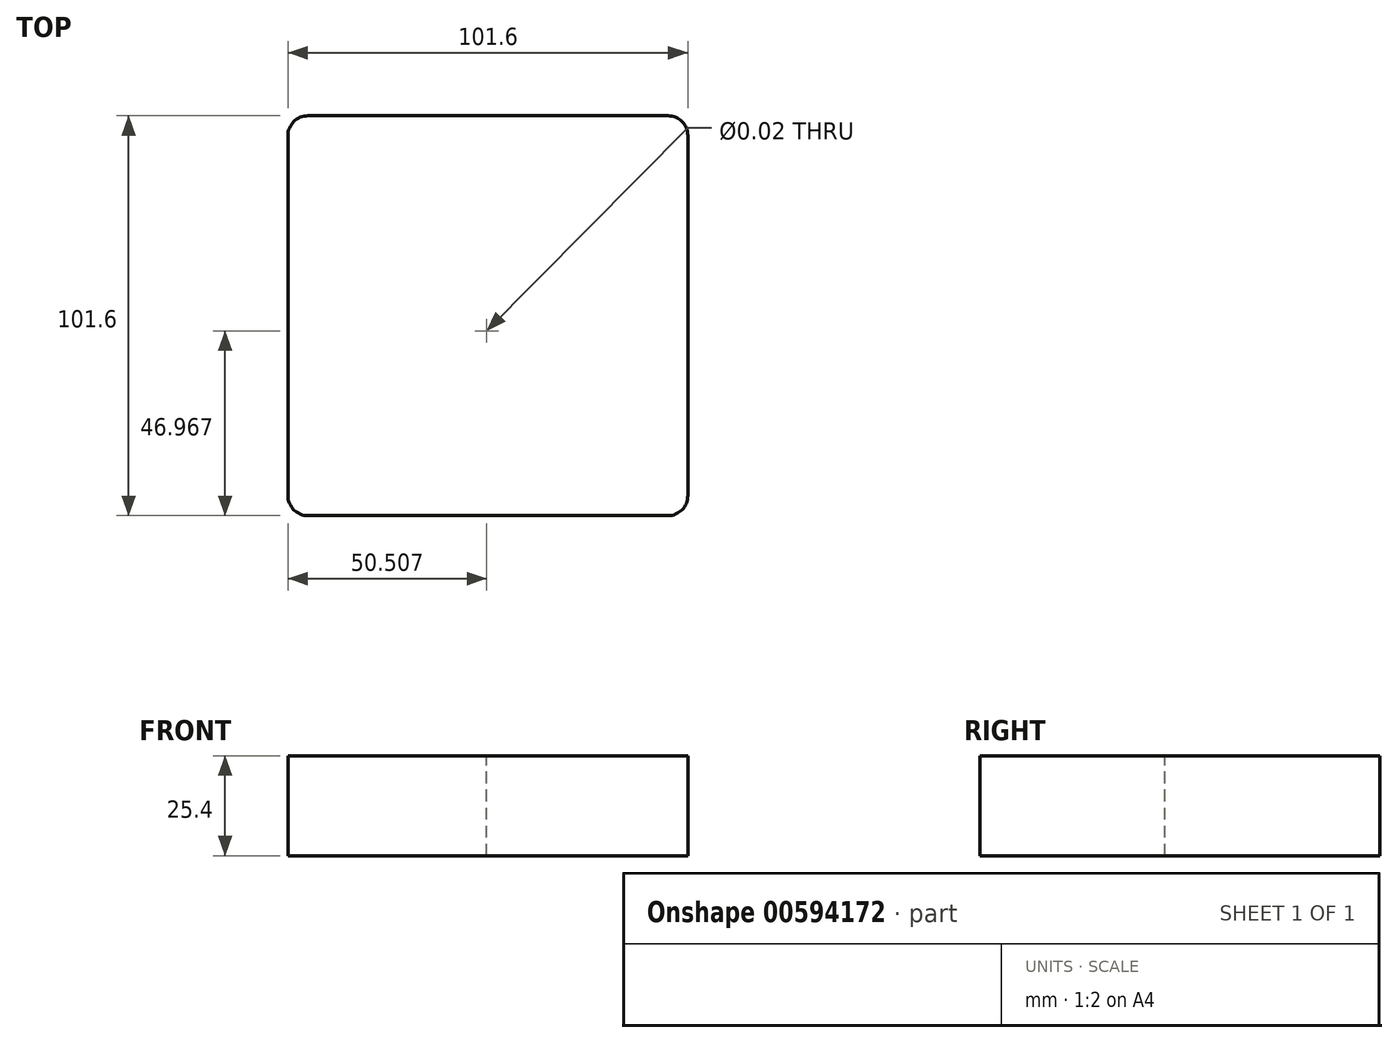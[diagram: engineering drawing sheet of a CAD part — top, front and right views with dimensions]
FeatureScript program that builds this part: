
annotation { "Feature Type Name" : "Feature", "Feature Type Description" : "" }
export const myFeature = defineFeature(function(context is Context, id is Id, definition is map)
    precondition{}
    {
        {
            var Q0;
            Q0=qCreatedBy(makeId("Top.planeOp"),FACE);
            var sketch = newSketch(context, id + "F0", { "sketchPlane" : qUnion([Q0])});
            skLineSegment(sketch, "E0.bottom", {"start": v(-75.45, 69.96) * mm, "end": v(26.15, 69.96) * mm});
            skLineSegment(sketch, "E0.top", {"start": v(-75.45, -31.64) * mm, "end": v(26.15, -31.64) * mm});
            skLineSegment(sketch, "E0.left", {"start": v(-75.45, 69.96) * mm, "end": v(-75.45, -31.64) * mm});
            skLineSegment(sketch, "E0.right", {"start": v(26.15, 69.96) * mm, "end": v(26.15, -31.64) * mm});
            skSolve(sketch);
        }
        {
            var Q0;
            Q0 = qSketchRegion(id + "F0", true);
            extrude(context, id + "F1", {"entities" : qUnion([Q0]), "depth" : 25.4 * mm, "offsetDistance" : 25.4 * mm});
        }
        {
            var Q0;
            Q0=makeQuery(id+"F1.opExtrude","SWEPT_EDGE",EDGE,{"disambiguationData":[OSD([sQuery(id+"F0.wireOp",EDGE,"E0.bottom"),sQuery(id+"F0.wireOp",EDGE,"E0.left")])]});
            fillet(context, id + "F2", {"entities" : qUnion([Q0]), "radius" : 5.08 * mm, "tangentPropagation" : true, "allowEdgeOverflow" : false});
        }
        {
            var Q0;
            Q0=makeQuery(id+"F1.opExtrude","SWEPT_EDGE",EDGE,{"disambiguationData":[OSD([sQuery(id+"F0.wireOp",EDGE,"E0.top"),sQuery(id+"F0.wireOp",EDGE,"E0.left")])]});
            fillet(context, id + "F3", {"entities" : qUnion([Q0]), "radius" : 5.08 * mm, "tangentPropagation" : true, "allowEdgeOverflow" : false});
        }
        {
            var Q0;
            Q0=makeQuery(id+"F1.opExtrude","SWEPT_EDGE",EDGE,{"disambiguationData":[OSD([sQuery(id+"F0.wireOp",EDGE,"E0.bottom"),sQuery(id+"F0.wireOp",EDGE,"E0.right")])]});
            fillet(context, id + "F4", {"entities" : qUnion([Q0]), "radius" : 5.08 * mm, "tangentPropagation" : true, "allowEdgeOverflow" : false});
        }
        {
            var Q0;
            Q0=makeQuery(id+"F1.opExtrude","SWEPT_EDGE",EDGE,{"disambiguationData":[OSD([sQuery(id+"F0.wireOp",EDGE,"E0.top"),sQuery(id+"F0.wireOp",EDGE,"E0.right")])]});
            fillet(context, id + "F5", {"entities" : qUnion([Q0]), "radius" : 5.08 * mm, "tangentPropagation" : true, "allowEdgeOverflow" : false});
        }
        {
            var Q0;
            Q0=makeQuery(id+"F1.opExtrude","CAP_FACE",FACE,{"disambiguationData":[OSD([sQuery(id+"F0.wireOp",EDGE,"E0.bottom"),sQuery(id+"F0.wireOp",EDGE,"E0.top"),sQuery(id+"F0.wireOp",EDGE,"E0.left"),sQuery(id+"F0.wireOp",EDGE,"E0.right")])],"isStart":false});
            var sketch = newSketch(context, id + "F6", { "sketchPlane" : qUnion([Q0])});
            skPoint(sketch, "E1", {"position": v(-24.94, 15.33) * mm});
            skSolve(sketch);
        }
        {
            var Q0;
            Q0=sQuery(id+"F6.wireOp",VERTEX,"E1");
            var Q1;
            Q1=makeQuery(id+"F1.opExtrude","SWEPT_BODY",BODY,{"disambiguationData":[OSD([sQuery(id+"F0.wireOp",EDGE,"E0.bottom"),sQuery(id+"F0.wireOp",EDGE,"E0.top"),sQuery(id+"F0.wireOp",EDGE,"E0.left"),sQuery(id+"F0.wireOp",EDGE,"E0.right")])]});
            hole(context, id + "F7", {"style" : HoleStyle.SIMPLE, "endStyle" : HoleEndStyle.THROUGH, "standardTappedOrClearance" : lookupTablePath({ "standard" : "ANSI", "size" : "13/32 (0.4)", "type" : "Drilled" }), "standardBlindInLast" : lookupTablePath({ "standard" : "ANSI", "size" : "13/32", "type" : "Drilled" }), "holeDiameter" : 13 / 812.8 * mm, "majorDiameter" : 6.35 * mm, "isTappedThrough" : true, "tappedDepth" : 12.7 * mm, "tapClearance" : 3, "locations" : qUnion([Q0]), "scope" : qUnion([Q1])});
        }
    });
